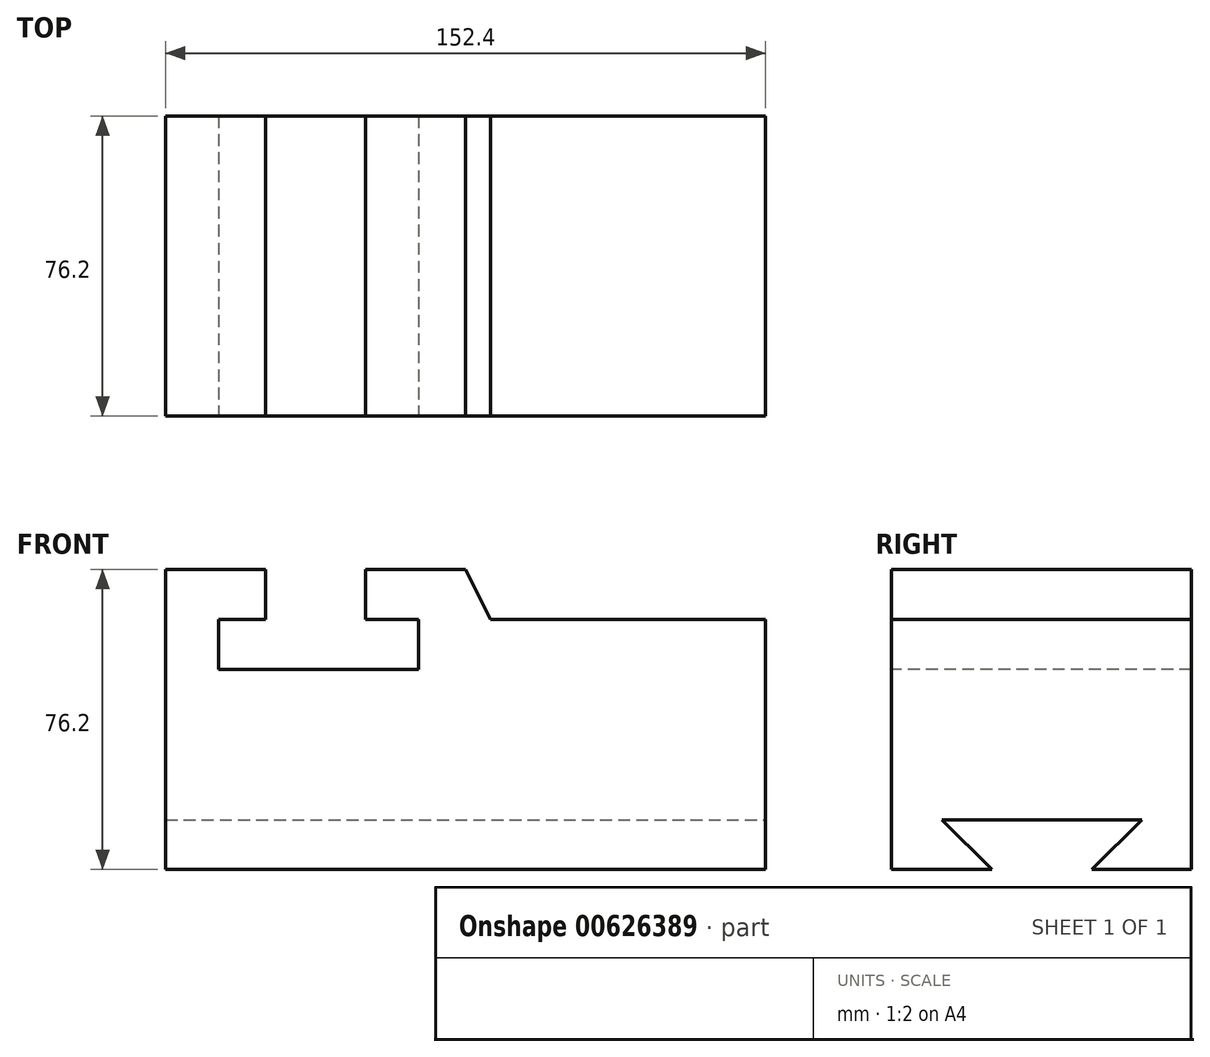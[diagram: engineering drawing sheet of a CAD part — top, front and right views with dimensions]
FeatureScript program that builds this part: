
annotation { "Feature Type Name" : "Feature", "Feature Type Description" : "" }
export const myFeature = defineFeature(function(context is Context, id is Id, definition is map)
    precondition{}
    {
        {
            var Q0;
            Q0=qCreatedBy(makeId("Front.planeOp"),FACE);
            var sketch = newSketch(context, id + "F0", { "sketchPlane" : qUnion([Q0])});
            skLineSegment(sketch, "E0", {"start": v(0, 0) * mm, "end": v(152.4, 0) * mm});
            skLineSegment(sketch, "E1", {"start": v(152.4, 0) * mm, "end": v(152.4, 76.2) * mm});
            skLineSegment(sketch, "E2", {"start": v(152.4, 76.2) * mm, "end": v(0, 76.2) * mm});
            skLineSegment(sketch, "E3", {"start": v(0, 76.2) * mm, "end": v(0, 0) * mm});
            skSolve(sketch);
        }
        {
            var Q0;
            Q0 = qSketchRegion(id + "F0", true);
            var Q1;
            Q1 = qSketchRegion(id + "FYK1UHCeUgwudgD_1", true);
            extrude(context, id + "F1", {"entities" : qUnion([Q0, Q1]), "oppositeDirection" : true, "depth" : 76.2 * mm, "offsetDistance" : 25.4 * mm});
        }
        {
            var Q0;
            Q0=makeQuery(id+"F1.opExtrude","SWEPT_FACE",FACE,{"disambiguationData":[OSD([sQuery(id+"F0.wireOp",EDGE,"E1")])]});
            var sketch = newSketch(context, id + "F2", { "sketchPlane" : qUnion([Q0])});
            skLineSegment(sketch, "E4", {"start": v(38.1, 0) * mm, "end": v(25.53, 0) * mm});
            skLineSegment(sketch, "E5", {"start": v(12.83, 12.57) * mm, "end": v(63.63, 12.57) * mm});
            skLineSegment(sketch, "E6", {"start": v(50.93, 0) * mm, "end": v(25.53, 0) * mm});
            skLineSegment(sketch, "E7", {"start": v(25.53, 0) * mm, "end": v(12.83, 12.57) * mm});
            skLineSegment(sketch, "E8", {"start": v(25.53, 0) * mm, "end": v(50.93, 0) * mm});
            skLineSegment(sketch, "E9", {"start": v(50.93, 0) * mm, "end": v(63.63, 12.57) * mm});
            skSolve(sketch);
        }
        {
            var Q0;
            Q0 = qSketchRegion(id + "F2", true);
            extrude(context, id + "F3", {"entities" : qUnion([Q0]), "operationType" : NewBodyOperationType.REMOVE, "oppositeDirection" : true, "depth" : 152.4 * mm, "offsetDistance" : 25.4 * mm});
        }
        {
            var Q0;
            Q0=makeQuery(id+"F1.opExtrude","CAP_FACE",FACE,{"disambiguationData":[OSD([sQuery(id+"F0.wireOp",EDGE,"E0"),sQuery(id+"F0.wireOp",EDGE,"E1"),sQuery(id+"F0.wireOp",EDGE,"E2"),sQuery(id+"F0.wireOp",EDGE,"E3")])],"isStart":true});
            var sketch = newSketch(context, id + "F4", { "sketchPlane" : qUnion([Q0])});
            skLineSegment(sketch, "E10", {"start": v(152.4, 76.2) * mm, "end": v(152.4, 63.5) * mm});
            skLineSegment(sketch, "E11", {"start": v(152.4, 63.5) * mm, "end": v(82.55, 63.5) * mm});
            skLineSegment(sketch, "E12", {"start": v(82.55, 63.5) * mm, "end": v(82.55, 76.2) * mm});
            skLineSegment(sketch, "E13", {"start": v(82.55, 76.2) * mm, "end": v(152.4, 76.2) * mm});
            skSolve(sketch);
        }
        {
            var Q0;
            Q0 = qSketchRegion(id + "F4", true);
            extrude(context, id + "F5", {"entities" : qUnion([Q0]), "operationType" : NewBodyOperationType.REMOVE, "oppositeDirection" : true, "depth" : 76.2 * mm, "offsetDistance" : 25.4 * mm});
        }
        {
            var Q0;
            Q0=makeQuery(id+"F1.opExtrude","CAP_FACE",FACE,{"disambiguationData":[OSD([sQuery(id+"F0.wireOp",EDGE,"E0"),sQuery(id+"F0.wireOp",EDGE,"E1"),sQuery(id+"F0.wireOp",EDGE,"E2"),sQuery(id+"F0.wireOp",EDGE,"E3")])],"isStart":true});
            var sketch = newSketch(context, id + "F6", { "sketchPlane" : qUnion([Q0])});
            skLineSegment(sketch, "E14", {"start": v(82.55, 63.5) * mm, "end": v(82.55, 76.2) * mm});
            skLineSegment(sketch, "E15", {"start": v(82.55, 76.2) * mm, "end": v(76.2, 76.2) * mm});
            skLineSegment(sketch, "E16", {"start": v(76.2, 76.2) * mm, "end": v(82.55, 63.5) * mm});
            skSolve(sketch);
        }
        {
            var Q0;
            Q0 = qSketchRegion(id + "F6", true);
            extrude(context, id + "F7", {"entities" : qUnion([Q0]), "operationType" : NewBodyOperationType.REMOVE, "oppositeDirection" : true, "depth" : 76.2 * mm, "offsetDistance" : 25.4 * mm});
        }
        {
            var Q0;
            Q0=makeQuery(id+"F1.opExtrude","CAP_FACE",FACE,{"disambiguationData":[OSD([sQuery(id+"F0.wireOp",EDGE,"E0"),sQuery(id+"F0.wireOp",EDGE,"E1"),sQuery(id+"F0.wireOp",EDGE,"E2"),sQuery(id+"F0.wireOp",EDGE,"E3")])],"isStart":true});
            var sketch = newSketch(context, id + "F8", { "sketchPlane" : qUnion([Q0])});
            skLineSegment(sketch, "E17", {"start": v(25.4, 76.2) * mm, "end": v(50.8, 76.2) * mm});
            skLineSegment(sketch, "E18", {"start": v(25.4, 76.2) * mm, "end": v(25.4, 63.5) * mm});
            skLineSegment(sketch, "E19", {"start": v(25.4, 63.5) * mm, "end": v(50.8, 63.5) * mm});
            skLineSegment(sketch, "E20", {"start": v(50.8, 63.5) * mm, "end": v(50.8, 76.2) * mm});
            skSolve(sketch);
        }
        {
            var Q0;
            Q0 = qSketchRegion(id + "F8", true);
            extrude(context, id + "F9", {"entities" : qUnion([Q0]), "operationType" : NewBodyOperationType.REMOVE, "oppositeDirection" : true, "depth" : 76.2 * mm, "offsetDistance" : 25.4 * mm});
        }
        {
            var Q0;
            Q0=makeQuery(id+"F1.opExtrude","CAP_FACE",FACE,{"disambiguationData":[OSD([sQuery(id+"F0.wireOp",EDGE,"E0"),sQuery(id+"F0.wireOp",EDGE,"E1"),sQuery(id+"F0.wireOp",EDGE,"E2"),sQuery(id+"F0.wireOp",EDGE,"E3")])],"isStart":true});
            var sketch = newSketch(context, id + "F10", { "sketchPlane" : qUnion([Q0])});
            skLineSegment(sketch, "E21", {"start": v(38.1, 63.5) * mm, "end": v(13.47, 63.5) * mm});
            skLineSegment(sketch, "E22", {"start": v(13.47, 63.5) * mm, "end": v(13.47, 50.8) * mm});
            skLineSegment(sketch, "E23", {"start": v(13.47, 50.8) * mm, "end": v(64.27, 50.8) * mm});
            skLineSegment(sketch, "E24", {"start": v(64.27, 50.8) * mm, "end": v(64.27, 63.5) * mm});
            skLineSegment(sketch, "E25", {"start": v(64.27, 63.5) * mm, "end": v(38.1, 63.5) * mm});
            skSolve(sketch);
        }
        {
            var Q0;
            Q0 = qSketchRegion(id + "F10", true);
            extrude(context, id + "F11", {"entities" : qUnion([Q0]), "operationType" : NewBodyOperationType.REMOVE, "oppositeDirection" : true, "depth" : 76.2 * mm, "offsetDistance" : 25.4 * mm});
        }
    });
